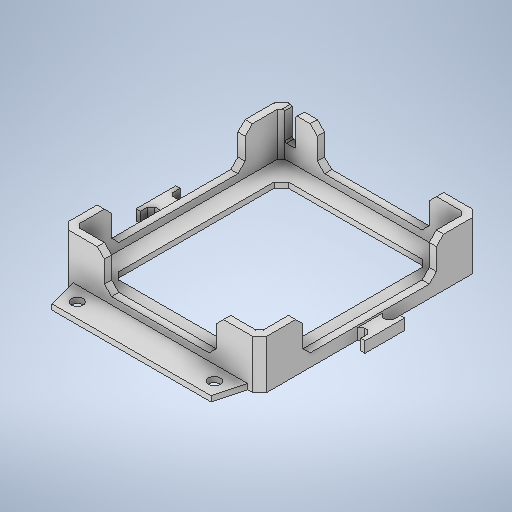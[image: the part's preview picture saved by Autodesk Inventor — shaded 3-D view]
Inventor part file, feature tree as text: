
AUTODESK INVENTOR PART (.ipt)
format: ipt  version: 2025.3 (Build 293356000, 356)  size: 417,280 bytes
history: native  units: mm
features: chamfer x6, extrude x5, sketch x3, other x1, mirror x1
ambient origin geometry x8: Origin, YZ Plane, XZ Plane, XY Plane, X Axis, Y Axis, Z Axis, Center Point
bodies: Body1 (feature_tree)
feature tree (16):
  other  "ソリッド1"
  sketch  "スケッチ1"
  extrude  "押し出し1"  Depth=51.0mm
  extrude  "押し出し2"  Depth=57.0mm
  extrude  "押し出し3"  Depth=2.0mm
  chamfer  "面取り1"  Distance=2.0mm
  chamfer  "面取り2"  Distance=5.0mm
  chamfer  "面取り4"  Distance=5.0mm
  chamfer  "面取り5"  Distance=38.0mm
  extrude  "押し出し4"  Depth=8.0mm
  chamfer  "面取り6"  Angle=75.0deg  [1 undecoded]
  extrude  "押し出し5"  Depth=3.2mm
  chamfer  "面取り7"  Distance=1.5mm
  mirror  "ミラー1"
  sketch  "スケッチ2"
  sketch  "スケッチ3"
note: 1 required parameter value undecoded (feature->parameter linkage not recoverable at this tier; creation-order binding heuristic only, values carry confidence <= 0.55)
